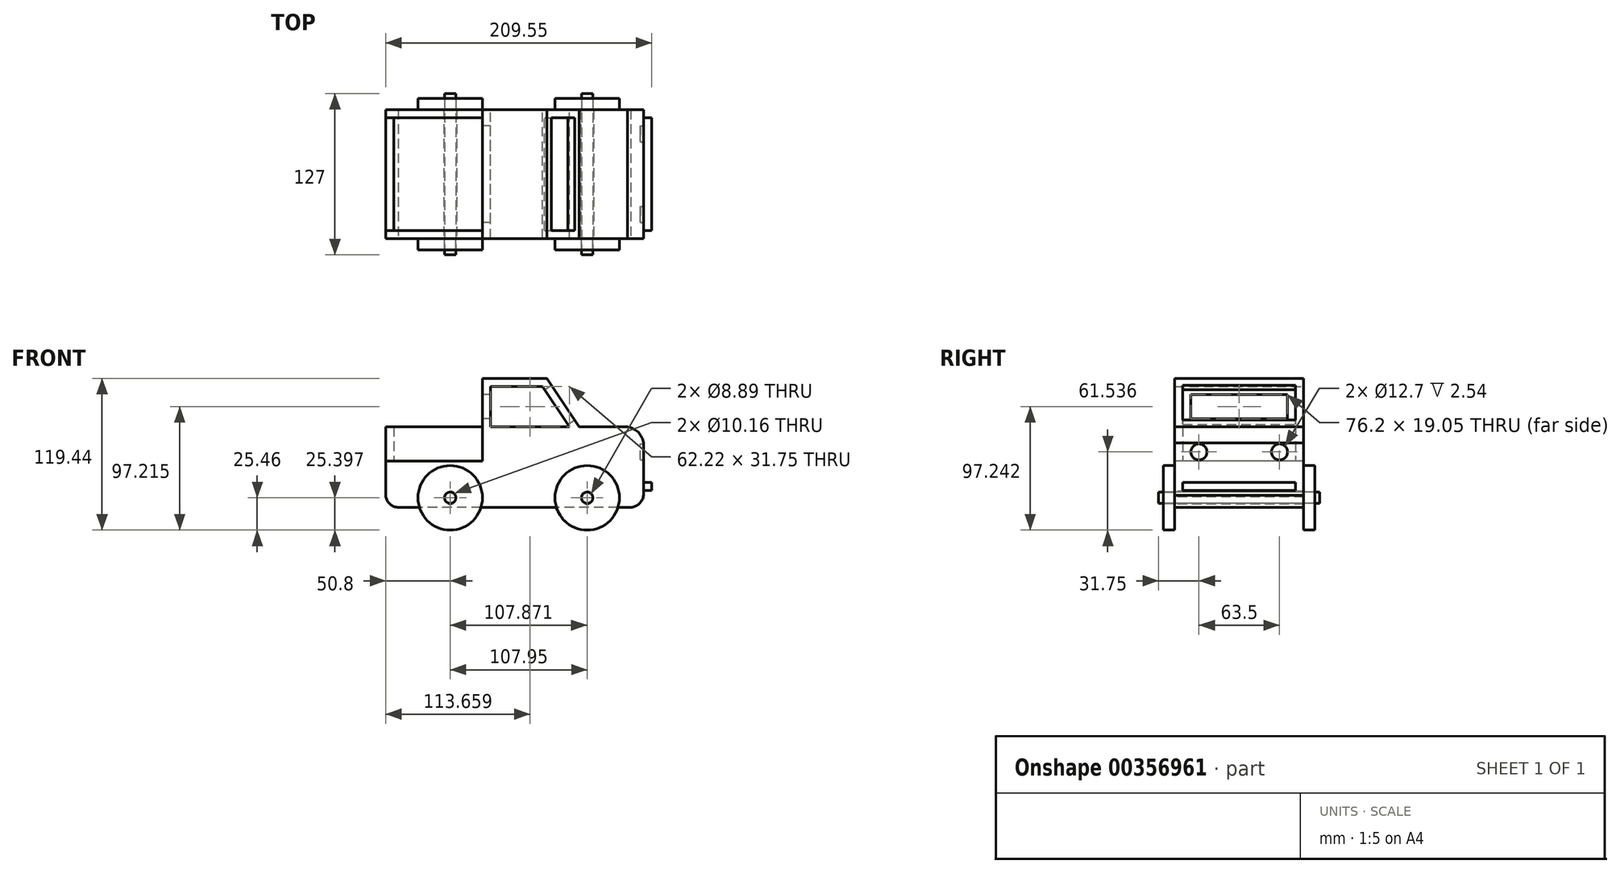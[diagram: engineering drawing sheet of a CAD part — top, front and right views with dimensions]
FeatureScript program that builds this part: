
annotation { "Feature Type Name" : "Feature", "Feature Type Description" : "" }
export const myFeature = defineFeature(function(context is Context, id is Id, definition is map)
    precondition{}
    {
        {
            var Q0;
            Q0=qCreatedBy(makeId("Front.planeOp"),FACE);
            var sketch = newSketch(context, id + "F0", { "sketchPlane" : qUnion([Q0])});
            skLineSegment(sketch, "E0.bottom", {"start": v(101.6, 50.8) * mm, "end": v(-101.6, 50.8) * mm});
            skLineSegment(sketch, "E0.top", {"start": v(101.6, -50.8) * mm, "end": v(-101.6, -50.8) * mm});
            skLineSegment(sketch, "E0.left", {"start": v(101.6, 50.8) * mm, "end": v(101.6, -50.8) * mm});
            skLineSegment(sketch, "E0.right", {"start": v(-101.6, 50.8) * mm, "end": v(-101.6, -50.8) * mm});
            skPoint(sketch, "E0.middle", {"position": v(0, 0) * mm});
            skSolve(sketch);
        }
        {
            var Q0;
            Q0 = qSketchRegion(id + "F0", true);
            extrude(context, id + "F1", {"entities" : qUnion([Q0]), "depth" : 101.6 * mm});
        }
        {
            var Q0;
            Q0=makeQuery(id+"F1.opExtrude","CAP_FACE",FACE,{"disambiguationData":[OSD([sQuery(id+"F0.wireOp",EDGE,"E0.bottom"),sQuery(id+"F0.wireOp",EDGE,"E0.top"),sQuery(id+"F0.wireOp",EDGE,"E0.left"),sQuery(id+"F0.wireOp",EDGE,"E0.right")])],"isStart":false});
            var sketch = newSketch(context, id + "F2", { "sketchPlane" : qUnion([Q0])});
            skLineSegment(sketch, "E1", {"start": v(101.6, 12.7) * mm, "end": v(50.8, 12.7) * mm});
            skLineSegment(sketch, "E2", {"start": v(50.8, 12.7) * mm, "end": v(25.4, 50.8) * mm});
            skLineSegment(sketch, "E3", {"start": v(-25.4, 50.8) * mm, "end": v(25.4, 50.8) * mm});
            skLineSegment(sketch, "E4", {"start": v(-25.4, 50.8) * mm, "end": v(-25.4, 12.7) * mm});
            skLineSegment(sketch, "E5", {"start": v(-25.4, 12.7) * mm, "end": v(-101.6, 12.7) * mm});
            skLineSegment(sketch, "E6", {"start": v(-101.6, 12.7) * mm, "end": v(-101.6, 50.8) * mm});
            skLineSegment(sketch, "E7", {"start": v(-101.6, 50.8) * mm, "end": v(-25.4, 50.8) * mm});
            skLineSegment(sketch, "E8", {"start": v(25.4, 50.8) * mm, "end": v(101.6, 50.8) * mm});
            skLineSegment(sketch, "E9", {"start": v(101.6, 50.8) * mm, "end": v(101.6, 12.7) * mm});
            skSolve(sketch);
        }
        {
            var Q0;
            Q0=makeQuery(id+"F2.imprint","IMPRINT",FACE,{"disambiguationData":[TD([[makeQuery(id+"F2.imprint","IMPRINT",EDGE,{"derivedFrom":sQuery(id+"F2.wireOp",EDGE,"E1")}),-1.0]])]});
            var Q1;
            Q1=makeQuery(id+"F2.imprint","IMPRINT",FACE,{"disambiguationData":[TD([[makeQuery(id+"F2.imprint","IMPRINT",EDGE,{"derivedFrom":sQuery(id+"F2.wireOp",EDGE,"E6")}),1.0]])]});
            var Q2;
            {var subQ3=sQuery(id+"F2.wireOp",EDGE,"Uotqzvim-ZrBp-Qglt-Cphv-QF7eFtVIwz87");Q2=makeQuery(id+"F2.imprint","IMPRINT",FACE,{"disambiguationData":[TD([[makeQuery(id+"F2.imprint","IMPRINT",EDGE,{"derivedFrom":subQ3}),-1.0]])]});}
            extrude(context, id + "F3", {"entities" : qUnion([Q0, Q1, Q2]), "operationType" : NewBodyOperationType.REMOVE, "endBound" : BoundingType.THROUGH_ALL, "oppositeDirection" : true, "depth" : 25.4 * mm});
        }
        {
            var Q0;
            Q0=makeQuery(id+"F1.opExtrude","CAP_FACE",FACE,{"disambiguationData":[OSD([sQuery(id+"F0.wireOp",EDGE,"E0.bottom"),sQuery(id+"F0.wireOp",EDGE,"E0.top"),sQuery(id+"F0.wireOp",EDGE,"E0.left"),sQuery(id+"F0.wireOp",EDGE,"E0.right")])],"isStart":false});
            var sketch = newSketch(context, id + "F4", { "sketchPlane" : qUnion([Q0])});
            skSolve(sketch);
        }
        {
            var Q0;
            Q0=makeQuery(id+"F1.opExtrude","CAP_FACE",FACE,{"disambiguationData":[OSD([sQuery(id+"F0.wireOp",EDGE,"E0.bottom"),sQuery(id+"F0.wireOp",EDGE,"E0.top"),sQuery(id+"F0.wireOp",EDGE,"E0.left"),sQuery(id+"F0.wireOp",EDGE,"E0.right")])],"isStart":true});
            var sketch = newSketch(context, id + "F5", { "sketchPlane" : qUnion([Q0])});
            skLineSegment(sketch, "E10", {"start": v(-43.17, 12.7) * mm, "end": v(-22, 44.45) * mm});
            skLineSegment(sketch, "E11", {"start": v(-22, 44.45) * mm, "end": v(19.05, 44.45) * mm});
            skLineSegment(sketch, "E12", {"start": v(19.05, 44.45) * mm, "end": v(19.05, 12.7) * mm});
            skLineSegment(sketch, "E13", {"start": v(19.05, 12.7) * mm, "end": v(-43.17, 12.7) * mm});
            skSolve(sketch);
        }
        {
            var Q0;
            Q0 = qSketchRegion(id + "F5", true);
            extrude(context, id + "F6", {"entities" : qUnion([Q0]), "operationType" : NewBodyOperationType.REMOVE, "endBound" : BoundingType.THROUGH_ALL, "oppositeDirection" : true, "depth" : 25.4 * mm});
        }
        {
            var Q0;
            Q0=makeQuery(id+"F3.boolean.opBoolean","COPY",FACE,{"derivedFrom":makeQuery(id+"F3.opExtrude","SWEPT_FACE",FACE,{"disambiguationData":[OSD([sQuery(id+"F2.wireOp",EDGE,"E2")])]})});
            var sketch = newSketch(context, id + "F7", { "sketchPlane" : qUnion([Q0])});
            skLineSegment(sketch, "E14.bottom", {"start": v(-95.25, 21.83) * mm, "end": v(-6.35, 21.83) * mm});
            skLineSegment(sketch, "E14.top", {"start": v(-95.25, -11.26) * mm, "end": v(-6.35, -11.26) * mm});
            skLineSegment(sketch, "E14.left", {"start": v(-95.25, 21.83) * mm, "end": v(-95.25, -11.26) * mm});
            skLineSegment(sketch, "E14.right", {"start": v(-6.35, 21.83) * mm, "end": v(-6.35, -11.26) * mm});
            skSolve(sketch);
        }
        {
            var Q0;
            Q0 = qSketchRegion(id + "F7", true);
            extrude(context, id + "F8", {"entities" : qUnion([Q0]), "operationType" : NewBodyOperationType.REMOVE, "oppositeDirection" : true, "depth" : 6.35 * mm});
        }
        {
            var Q0;
            Q0=makeQuery(id+"F3.boolean.opBoolean","COPY",FACE,{"derivedFrom":makeQuery(id+"F3.opExtrude","SWEPT_FACE",FACE,{"disambiguationData":[OSD([sQuery(id+"F2.wireOp",EDGE,"E4")])]})});
            var sketch = newSketch(context, id + "F9", { "sketchPlane" : qUnion([Q0])});
            skLineSegment(sketch, "E15.bottom", {"start": v(88.9, 38.13) * mm, "end": v(12.7, 38.13) * mm});
            skLineSegment(sketch, "E15.top", {"start": v(88.9, 19.08) * mm, "end": v(12.7, 19.08) * mm});
            skLineSegment(sketch, "E15.left", {"start": v(88.9, 38.13) * mm, "end": v(88.9, 19.08) * mm});
            skLineSegment(sketch, "E15.right", {"start": v(12.7, 38.13) * mm, "end": v(12.7, 19.08) * mm});
            skPoint(sketch, "E15.middle", {"position": v(50.8, 28.6) * mm});
            skPoint(sketch, "E15.middle.positionSnap0", {"position": v(50.8, 12.7) * mm});
            skPoint(sketch, "E15.centerSnap0", {"position": v(50.8, 12.7) * mm});
            skSolve(sketch);
        }
        {
            var Q0;
            Q0 = qSketchRegion(id + "F9", true);
            extrude(context, id + "F10", {"entities" : qUnion([Q0]), "operationType" : NewBodyOperationType.REMOVE, "oppositeDirection" : true, "depth" : 6.35 * mm});
        }
        {
            var Q0;
            Q0=makeQuery(id+"F4.imprint","IMPRINT",FACE,{"disambiguationData":[TD([[makeQuery(id+"F4.imprint","IMPRINT",EDGE,{"derivedFrom":makeQuery(id+"F1.opExtrude","CAP_EDGE",EDGE,{"disambiguationData":[OSD([sQuery(id+"F0.wireOp",EDGE,"E0.top")])],"isStart":false})}),-1.0]])]});
            var sketch = newSketch(context, id + "F11", { "sketchPlane" : qUnion([Q0])});
            skCircle(sketch, "E16", {"center": v(-50.8, -43.18) * mm, "radius": 5.08 * mm});
            skCircle(sketch, "E17", {"center": v(57.07, -43.18) * mm, "radius": 5.08 * mm});
            skSolve(sketch);
        }
        {
            var Q0;
            Q0 = qSketchRegion(id + "F11", true);
            extrude(context, id + "F12", {"entities" : qUnion([Q0]), "operationType" : NewBodyOperationType.REMOVE, "endBound" : BoundingType.THROUGH_ALL, "oppositeDirection" : true, "depth" : 25.4 * mm});
        }
        {
            var Q0;
            Q0=makeQuery(id+"F1.opExtrude","CAP_FACE",FACE,{"disambiguationData":[OSD([sQuery(id+"F0.wireOp",EDGE,"E0.bottom"),sQuery(id+"F0.wireOp",EDGE,"E0.top"),sQuery(id+"F0.wireOp",EDGE,"E0.left"),sQuery(id+"F0.wireOp",EDGE,"E0.right")])],"isStart":false});
            var sketch = newSketch(context, id + "F13", { "sketchPlane" : qUnion([Q0])});
            skArc(sketch, "E18", {"start": v(101.6, 0) * mm, "mid": v(95.52, 9.96) * mm, "end": v(84.19, 12.7) * mm});
            skLineSegment(sketch, "E19", {"start": v(84.19, 12.7) * mm, "end": v(101.6, 12.7) * mm});
            skLineSegment(sketch, "E20", {"start": v(101.6, 12.7) * mm, "end": v(101.6, 0) * mm});
            skSolve(sketch);
        }
        {
            var Q0;
            Q0 = qSketchRegion(id + "F13", true);
            extrude(context, id + "F14", {"entities" : qUnion([Q0]), "operationType" : NewBodyOperationType.REMOVE, "endBound" : BoundingType.THROUGH_ALL, "oppositeDirection" : true, "depth" : 25.4 * mm});
        }
        {
            var Q0;
            Q0=makeQuery(id+"F1.opExtrude","CAP_FACE",FACE,{"disambiguationData":[OSD([sQuery(id+"F0.wireOp",EDGE,"E0.bottom"),sQuery(id+"F0.wireOp",EDGE,"E0.top"),sQuery(id+"F0.wireOp",EDGE,"E0.left"),sQuery(id+"F0.wireOp",EDGE,"E0.right")])],"isStart":false});
            var sketch = newSketch(context, id + "F15", { "sketchPlane" : qUnion([Q0])});
            skArc(sketch, "E21", {"start": v(-101.6, -38.48) * mm, "mid": v(-99.34, -47.12) * mm, "end": v(-91.2, -50.8) * mm});
            skArc(sketch, "E22", {"start": v(89.76, -50.8) * mm, "mid": v(98.73, -47.27) * mm, "end": v(101.6, -38.07) * mm});
            skSolve(sketch);
        }
        {
            var Q0;
            Q0 = qSketchRegion(id + "F15", true);
            var Q1;
            {var subQ0=sQuery(id+"F15.wireOp",EDGE,"E21");var subQ1=sQuery(id+"F0.wireOp",EDGE,"E0.right");var subQ2=makeQuery(id+"F1.opExtrude","CAP_EDGE",EDGE,{"disambiguationData":[OSD([subQ1])],"isStart":false});var subQ3=makeQuery(id+"F15.imprint","INTERSECT",VERTEX,{"disambiguationData":[OD(1.0)],"derivedFrom":[subQ2,subQ0]});Q1=makeQuery(id+"F15.imprint","IMPRINT",FACE,{"disambiguationData":[TD([[makeQuery(id+"F15.imprint","IMPRINT",EDGE,{"disambiguationData":[TD([[subQ3,-1.0]])],"derivedFrom":subQ0}),-1.0]])]});}
            var Q2;
            {var subQ0=sQuery(id+"F15.wireOp",EDGE,"E22");var subQ1=sQuery(id+"F0.wireOp",EDGE,"E0.left");var subQ5=makeQuery(id+"F1.opExtrude","CAP_EDGE",EDGE,{"disambiguationData":[OSD([subQ1])],"isStart":false});var subQ6=makeQuery(id+"F15.imprint","INTERSECT",VERTEX,{"disambiguationData":[OD(1.0)],"derivedFrom":[subQ5,subQ0]});Q2=makeQuery(id+"F15.imprint","IMPRINT",FACE,{"disambiguationData":[TD([[makeQuery(id+"F15.imprint","IMPRINT",EDGE,{"disambiguationData":[TD([[subQ6,1.0]])],"derivedFrom":subQ0}),-1.0]])]});}
            extrude(context, id + "F16", {"entities" : qUnion([Q0, Q1, Q2]), "operationType" : NewBodyOperationType.REMOVE, "endBound" : BoundingType.THROUGH_ALL, "oppositeDirection" : true, "depth" : 25.4 * mm});
        }
        {
            var Q0;
            Q0=makeQuery(id+"F4.imprint","IMPRINT",FACE,{"disambiguationData":[TD([[makeQuery(id+"F4.imprint","IMPRINT",EDGE,{"derivedFrom":makeQuery(id+"F1.opExtrude","CAP_EDGE",EDGE,{"disambiguationData":[OSD([sQuery(id+"F0.wireOp",EDGE,"E0.top")])],"isStart":false})}),-1.0]])]});
            var sketch = newSketch(context, id + "F17", { "sketchPlane" : qUnion([Q0])});
            skCircle(sketch, "E23", {"center": v(-50.8, -43.24) * mm, "radius": 4.45 * mm});
            skCircle(sketch, "E24", {"center": v(57.15, -43.24) * mm, "radius": 4.45 * mm});
            skCircle(sketch, "E25", {"center": v(-50.8, -43.24) * mm, "radius": 25.4 * mm});
            skCircle(sketch, "E26", {"center": v(57.15, -43.24) * mm, "radius": 25.4 * mm});
            skSolve(sketch);
        }
        {
            var Q0;
            Q0 = qSketchRegion(id + "F17", true);
            extrude(context, id + "F18", {"entities" : qUnion([Q0]), "depth" : 8.9 * mm});
        }
        {
            var Q0;
            Q0=makeQuery(id+"F17.imprint","IMPRINT",FACE,{"disambiguationData":[TD([[makeQuery(id+"F17.imprint","IMPRINT",EDGE,{"derivedFrom":sQuery(id+"F17.wireOp",EDGE,"E23")}),1.0]])]});
            var Q1;
            Q1=makeQuery(id+"F17.imprint","IMPRINT",FACE,{"disambiguationData":[TD([[makeQuery(id+"F17.imprint","IMPRINT",EDGE,{"derivedFrom":sQuery(id+"F17.wireOp",EDGE,"E24")}),1.0]])]});
            extrude(context, id + "F19", {"entities" : qUnion([Q0, Q1]), "oppositeDirection" : true, "depth" : 114.3 * mm, "hasSecondDirection" : true, "secondDirectionOppositeDirection" : false, "secondDirectionDepth" : 12.7 * mm});
        }
        {
            var Q0;
            Q0=makeQuery(id+"F1.opExtrude","CAP_FACE",FACE,{"disambiguationData":[OSD([sQuery(id+"F0.wireOp",EDGE,"E0.bottom"),sQuery(id+"F0.wireOp",EDGE,"E0.top"),sQuery(id+"F0.wireOp",EDGE,"E0.left"),sQuery(id+"F0.wireOp",EDGE,"E0.right")])],"isStart":true});
            var sketch = newSketch(context, id + "F20", { "sketchPlane" : qUnion([Q0])});
            skCircle(sketch, "E27", {"center": v(-57.07, -43.18) * mm, "radius": 25.4 * mm});
            skCircle(sketch, "E28", {"center": v(50.8, -43.18) * mm, "radius": 25.4 * mm});
            skSolve(sketch);
        }
        {
            var Q0;
            Q0 = qSketchRegion(id + "F20", true);
            extrude(context, id + "F21", {"entities" : qUnion([Q0]), "depth" : 8.9 * mm});
        }
        {
            var Q0;
            Q0=makeQuery(id+"F1.opExtrude","SWEPT_FACE",FACE,{"disambiguationData":[OSD([sQuery(id+"F0.wireOp",EDGE,"E0.left")])]});
            var sketch = newSketch(context, id + "F22", { "sketchPlane" : qUnion([Q0])});
            skCircle(sketch, "E29", {"center": v(-82.55, -7.1) * mm, "radius": 6.35 * mm});
            skCircle(sketch, "E30", {"center": v(-19.05, -7.1) * mm, "radius": 6.35 * mm});
            skLineSegment(sketch, "E31.bottom", {"start": v(-95.25, -31.11) * mm, "end": v(-6.35, -31.11) * mm});
            skLineSegment(sketch, "E31.top", {"start": v(-95.25, -37.46) * mm, "end": v(-6.35, -37.46) * mm});
            skLineSegment(sketch, "E31.left", {"start": v(-95.25, -31.11) * mm, "end": v(-95.25, -37.46) * mm});
            skLineSegment(sketch, "E31.right", {"start": v(-6.35, -31.11) * mm, "end": v(-6.35, -37.46) * mm});
            skSolve(sketch);
        }
        {
            var Q0;
            Q0=makeQuery(id+"F22.imprint","IMPRINT",FACE,{"disambiguationData":[TD([[makeQuery(id+"F22.imprint","IMPRINT",EDGE,{"derivedFrom":sQuery(id+"F22.wireOp",EDGE,"E31.bottom")}),-1.0]])]});
            extrude(context, id + "F23", {"entities" : qUnion([Q0]), "depth" : 6.35 * mm});
        }
        {
            var Q0;
            Q0=makeQuery(id+"F22.imprint","IMPRINT",FACE,{"disambiguationData":[TD([[makeQuery(id+"F22.imprint","IMPRINT",EDGE,{"derivedFrom":sQuery(id+"F22.wireOp",EDGE,"E29")}),1.0]])]});
            var Q1;
            Q1=makeQuery(id+"F22.imprint","IMPRINT",FACE,{"disambiguationData":[TD([[makeQuery(id+"F22.imprint","IMPRINT",EDGE,{"derivedFrom":sQuery(id+"F22.wireOp",EDGE,"E30")}),1.0]])]});
            extrude(context, id + "F24", {"entities" : qUnion([Q0, Q1]), "operationType" : NewBodyOperationType.REMOVE, "oppositeDirection" : true, "depth" : 2.54 * mm});
        }
        {
            var Q0;
            Q0=makeQuery(id+"F4.imprint","IMPRINT",FACE,{"disambiguationData":[TD([[makeQuery(id+"F4.imprint","IMPRINT",EDGE,{"derivedFrom":makeQuery(id+"F1.opExtrude","CAP_EDGE",EDGE,{"disambiguationData":[OSD([sQuery(id+"F0.wireOp",EDGE,"E0.top")])],"isStart":false})}),-1.0]])]});
            var sketch = newSketch(context, id + "F25", { "sketchPlane" : qUnion([Q0])});
            skLineSegment(sketch, "E32", {"start": v(-25.4, 12.7) * mm, "end": v(-25.4, -14.2) * mm});
            skLineSegment(sketch, "E33", {"start": v(-25.4, -14.2) * mm, "end": v(-101.6, -14.2) * mm});
            skLineSegment(sketch, "E34", {"start": v(-101.6, -14.2) * mm, "end": v(-101.6, 12.7) * mm});
            skLineSegment(sketch, "E35", {"start": v(-101.6, 12.7) * mm, "end": v(-25.4, 12.7) * mm});
            skSolve(sketch);
        }
        {
            var Q0;
            Q0 = qSketchRegion(id + "F25", true);
            extrude(context, id + "F26", {"entities" : qUnion([Q0]), "operationType" : NewBodyOperationType.REMOVE, "endBound" : BoundingType.THROUGH_ALL, "oppositeDirection" : true, "depth" : 25.4 * mm});
        }
        {
            var Q0;
            Q0=makeQuery(id+"F26.boolean.opBoolean","COPY",FACE,{"derivedFrom":makeQuery(id+"F26.opExtrude","SWEPT_FACE",FACE,{"disambiguationData":[OSD([sQuery(id+"F25.wireOp",EDGE,"E32")])]})});
            var sketch = newSketch(context, id + "F27", { "sketchPlane" : qUnion([Q0])});
            skLineSegment(sketch, "E36.bottom", {"start": v(0, 12.7) * mm, "end": v(6.35, 12.7) * mm});
            skLineSegment(sketch, "E36.top", {"start": v(0, -14.2) * mm, "end": v(6.35, -14.2) * mm});
            skLineSegment(sketch, "E36.left", {"start": v(0, 12.7) * mm, "end": v(0, -14.2) * mm});
            skLineSegment(sketch, "E36.right", {"start": v(6.35, 12.7) * mm, "end": v(6.35, -14.2) * mm});
            skLineSegment(sketch, "E37.bottom", {"start": v(101.6, 12.7) * mm, "end": v(95.25, 12.7) * mm});
            skLineSegment(sketch, "E37.top", {"start": v(101.6, -14.2) * mm, "end": v(95.25, -14.2) * mm});
            skLineSegment(sketch, "E37.left", {"start": v(101.6, 12.7) * mm, "end": v(101.6, -14.2) * mm});
            skLineSegment(sketch, "E37.right", {"start": v(95.25, 12.7) * mm, "end": v(95.25, -14.2) * mm});
            skSolve(sketch);
        }
        {
            var Q0;
            Q0 = qSketchRegion(id + "F27", true);
            extrude(context, id + "F28", {"entities" : qUnion([Q0]), "depth" : 76.2 * mm});
        }
        {
            var Q0;
            Q0=makeQuery(id+"F26.boolean.opBoolean","COPY",FACE,{"derivedFrom":makeQuery(id+"F26.opExtrude","SWEPT_FACE",FACE,{"disambiguationData":[OSD([sQuery(id+"F25.wireOp",EDGE,"E33")])]})});
            var sketch = newSketch(context, id + "F29", { "sketchPlane" : qUnion([Q0])});
            skLineSegment(sketch, "E38.bottom", {"start": v(-101.6, -6.35) * mm, "end": v(-95.25, -6.35) * mm});
            skLineSegment(sketch, "E38.top", {"start": v(-101.6, -95.25) * mm, "end": v(-95.25, -95.25) * mm});
            skLineSegment(sketch, "E38.left", {"start": v(-101.6, -6.35) * mm, "end": v(-101.6, -95.25) * mm});
            skLineSegment(sketch, "E38.right", {"start": v(-95.25, -6.35) * mm, "end": v(-95.25, -95.25) * mm});
            skSolve(sketch);
        }
        {
            var Q0;
            Q0 = qSketchRegion(id + "F29", true);
            extrude(context, id + "F30", {"entities" : qUnion([Q0]), "depth" : 26.9 * mm});
        }
    });
